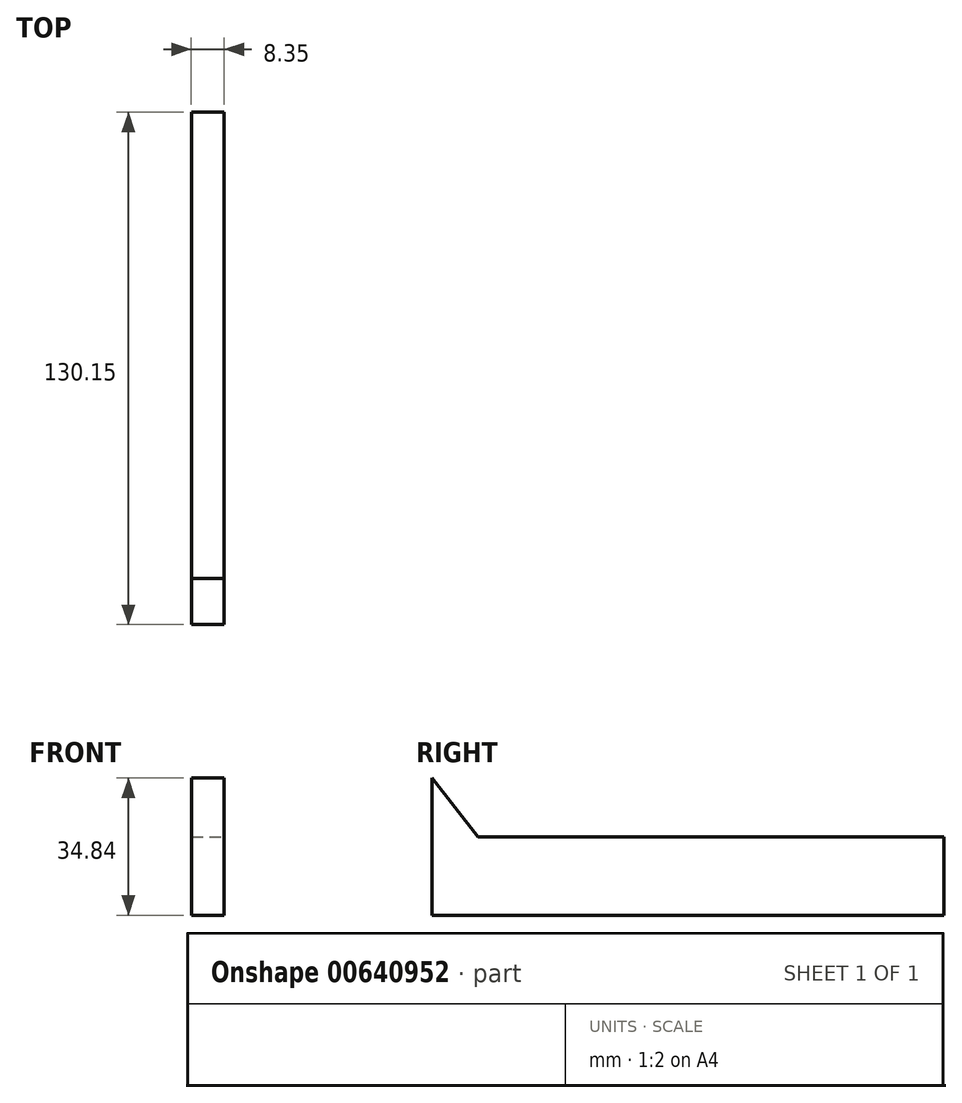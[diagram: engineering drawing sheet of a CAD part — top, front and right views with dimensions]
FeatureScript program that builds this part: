
annotation { "Feature Type Name" : "Feature", "Feature Type Description" : "" }
export const myFeature = defineFeature(function(context is Context, id is Id, definition is map)
    precondition{}
    {
        {
            var Q0;
            Q0=qCreatedBy(makeId("Top.planeOp"),FACE);
            var sketch = newSketch(context, id + "F0", { "sketchPlane" : qUnion([Q0])});
            skLineSegment(sketch, "E0.bottom", {"start": v(5.6, 31.62) * mm, "end": v(13.94, 31.62) * mm});
            skLineSegment(sketch, "E0.top", {"start": v(5.6, -33.53) * mm, "end": v(13.94, -33.53) * mm});
            skLineSegment(sketch, "E0.left", {"start": v(5.6, 31.62) * mm, "end": v(5.6, -33.53) * mm});
            skLineSegment(sketch, "E0.right", {"start": v(13.94, 31.62) * mm, "end": v(13.94, -33.53) * mm});
            skSolve(sketch);
        }
        {
            var Q0;
            Q0=makeQuery(id+"F0.imprint","IMPRINT",FACE,{"disambiguationData":[TD([[makeQuery(id+"F0.imprint","IMPRINT",EDGE,{"derivedFrom":sQuery(id+"F0.wireOp",EDGE,"E0.bottom")}),-1.0]])]});
            extrude(context, id + "F1", {"entities" : qUnion([Q0]), "depth" : 19.84 * mm, "offsetDistance" : 25 * mm});
        }
        {
            var Q0;
            Q0=makeQuery(id+"F1.opExtrude","CAP_FACE",FACE,{"disambiguationData":[OSD([sQuery(id+"F0.wireOp",EDGE,"E0.bottom"),sQuery(id+"F0.wireOp",EDGE,"E0.top"),sQuery(id+"F0.wireOp",EDGE,"E0.left"),sQuery(id+"F0.wireOp",EDGE,"E0.right")])],"isStart":false});
            var sketch = newSketch(context, id + "F2", { "sketchPlane" : qUnion([Q0])});
            skLineSegment(sketch, "E1.bottom", {"start": v(5.6, -21.83) * mm, "end": v(13.94, -21.83) * mm});
            skLineSegment(sketch, "E1.top", {"start": v(5.6, -33.53) * mm, "end": v(13.94, -33.53) * mm});
            skLineSegment(sketch, "E1.left", {"start": v(5.6, -21.83) * mm, "end": v(5.6, -33.53) * mm});
            skLineSegment(sketch, "E1.right", {"start": v(13.94, -21.83) * mm, "end": v(13.94, -33.53) * mm});
            skSolve(sketch);
        }
        {
            var Q0;
            Q0=makeQuery(id+"F2.imprint","IMPRINT",FACE,{"disambiguationData":[TD([[makeQuery(id+"F2.imprint","IMPRINT",EDGE,{"derivedFrom":sQuery(id+"F2.wireOp",EDGE,"E1.bottom")}),-1.0]])]});
            extrude(context, id + "F3", {"entities" : qUnion([Q0]), "operationType" : NewBodyOperationType.ADD, "depth" : 15 * mm, "offsetDistance" : 25 * mm});
        }
        {
            var Q1;
            Q1=makeQuery(id+"F3.opExtrude","CAP_FACE",FACE,{"disambiguationData":[OSD([sQuery(id+"F2.wireOp",EDGE,"E1.bottom"),sQuery(id+"F2.wireOp",EDGE,"E1.top"),sQuery(id+"F2.wireOp",EDGE,"E1.left"),sQuery(id+"F2.wireOp",EDGE,"E1.right")])],"isStart":false});
            var Q2;
            Q2=makeQuery(id+"F1.opExtrude","CAP_FACE",FACE,{"disambiguationData":[OSD([sQuery(id+"F0.wireOp",EDGE,"E0.bottom"),sQuery(id+"F0.wireOp",EDGE,"E0.top"),sQuery(id+"F0.wireOp",EDGE,"E0.left"),sQuery(id+"F0.wireOp",EDGE,"E0.right")])],"isStart":false});
            loft(context, id + "F4", {"operationType" : NewBodyOperationType.REMOVE, "sheetProfilesArray" : [{ "sheetProfileEntities" : qUnion([Q1]) }, { "sheetProfileEntities" : qUnion([Q2]) }]});
        }
        {
            var Q0;
            Q0=makeQuery(id+"F1.opExtrude","SWEPT_FACE",FACE,{"disambiguationData":[OSD([sQuery(id+"F0.wireOp",EDGE,"E0.bottom")])]});
            extrude(context, id + "F5", {"entities" : qUnion([Q0]), "operationType" : NewBodyOperationType.ADD, "depth" : 65 * mm, "offsetDistance" : 25 * mm});
        }
    });
